AUTODESK INVENTOR PART (.ipt)
format: ipt  version: 2022.1 (Build 261234000, 234)  size: 580,608 bytes
history: native  units: mm (DEFAULTED — no unit token found)
features: other x8, sketch x4, reference x2, extrude x1, hole x1, plane x1, projected_geometry x1
ambient origin geometry x8: Origin, YZ Plane, XZ Plane, XY Plane, X Axis, Y Axis, Z Axis, Center Point
bodies: Solid1 (feature_tree), Solid3 (feature_tree)
feature tree (18):
  parser-record x1  (decoder bookkeeping rows leaked as tree rows — omitted from the tree; the rows remain in map.json)
  other  "Driven Length"
  other  "Plano inicial"
  other  "Plano final"
  extrude  "Cuerpo"  TaperAngle=0.0deg  [1 undecoded]
  hole  "Agujero1"  [1 undecoded]
  sketch  "Boceto"  dims[d12=5.0mm d13=10.0mm d14=470.0mm d15=20.0mm d16=20.0mm d17=90.0deg d18=460.0mm d19=11.0mm d20=20.0mm d21=4.0mm d22=2.0mm d23=90.0deg d24=8.0mm d25=20.594885mm]
  sketch  "Sketch3"  dims[d3=460.0mm d4=0.0mm]
  plane  "Work Plane3"
  sketch  "Sketch4"  dims[d7=7.5mm d10=40.0mm]
  sketch  "Boceto5"  dims[d11=40.0mm]
  reference  "Referencia1"
  projected_geometry  "Contorno proyectado1"
  reference  "Referencia2"
  other  "Srf2"
  other  "<userpath>\Desktop\PDM\ProyectoRobotPallet\RobotPallet.iam"
  other  "RobotPallet.iam"
  other  "PlanchaBaseInferior:1"
note: 2 required parameter values undecoded (feature->parameter linkage not recoverable at this tier; creation-order binding heuristic only, values carry confidence <= 0.55)
